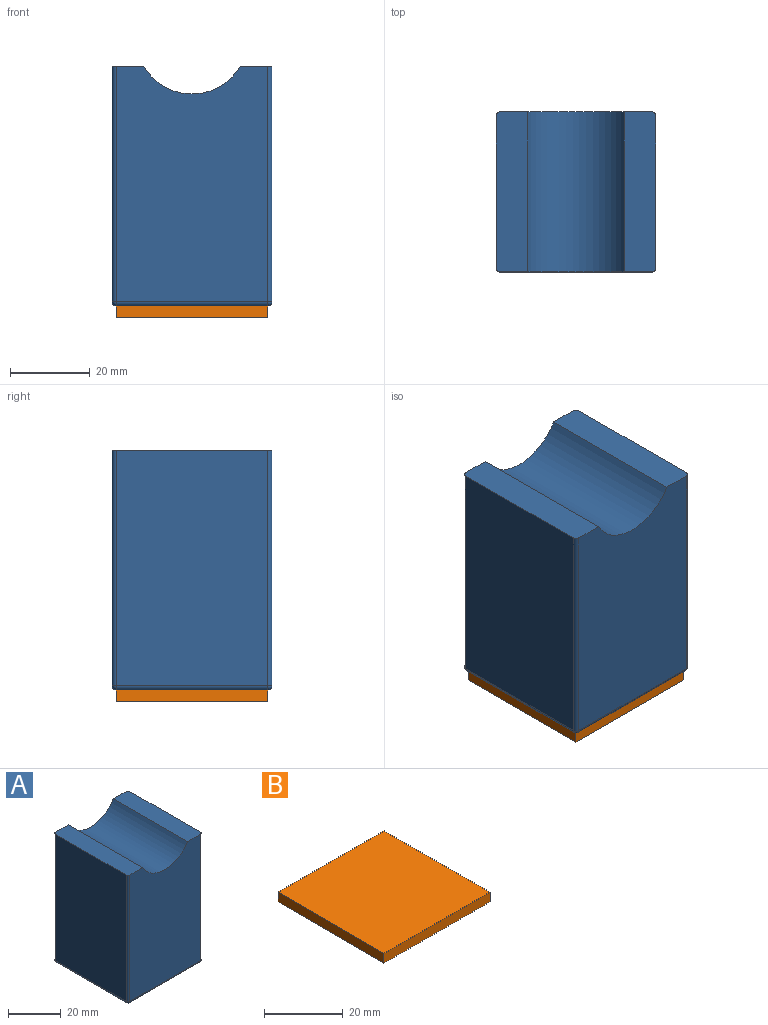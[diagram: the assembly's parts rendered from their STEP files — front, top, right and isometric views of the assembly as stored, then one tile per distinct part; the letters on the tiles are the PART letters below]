
ASSEMBLY  parts=2 mates=1
PART A: 20 faces, bbox 40x40x60 mm
  f0: plane 40x7.88mm, normal (0,0,1), area 314.6mm2, adj f1,f2,f4,f7,f13,f19
  f1: plane 59x38mm, normal (0,1,0), area 2121.6mm2, adj f0,f5,f7,f10,f16,f19
  f2: plane 59x38mm, normal (1,0,0), area 2242mm2, adj f0,f13,f17,f19
  f3: plane 59x38mm, normal (-1,0,0), area 2242mm2, adj f5,f8,f10,f11
  f4: plane 59x38mm, normal (0,-1,0), area 2121.6mm2, adj f0,f5,f7,f8,f12,f13
  f5: plane 40x7.88mm, normal (0,0,1), area 314.6mm2, adj f1,f3,f4,f7,f8,f10
  f6: plane 38x38mm, normal (0,0,-1), area 1444mm2, adj f11,f12,f16,f17
  f7: cylinder r=14mm len=40mm, axis (0,-1,0), area 1172.9mm2, adj f0,f1,f4,f5
  f8: cylinder r=1mm len=59mm, axis (0,0,1), area 92.7mm2, adj f3,f4,f5,f9
  f9: sphere r=1mm, area 1.6mm2, adj f8,f11,f12
  f10: cylinder r=1mm len=59mm, axis (0,0,-1), area 92.7mm2, adj f1,f3,f5,f14
  f11: cylinder r=1mm len=38mm, axis (0,-1,0), area 59.7mm2, adj f3,f6,f9,f14
  f12: cylinder r=1mm len=38mm, axis (1,0,0), area 59.7mm2, adj f4,f6,f9,f15
  f13: cylinder r=1mm len=59mm, axis (0,0,-1), area 92.7mm2, adj f0,f2,f4,f15
  f14: sphere r=1mm, area 1.6mm2, adj f10,f11,f16
  f15: sphere r=1mm, area 1.6mm2, adj f12,f13,f17
  f16: cylinder r=1mm len=38mm, axis (-1,0,0), area 59.7mm2, adj f1,f6,f14,f18
  f17: cylinder r=1mm len=38mm, axis (0,1,0), area 59.7mm2, adj f2,f6,f15,f18
  f18: sphere r=1mm, area 1.6mm2, adj f16,f17,f19
  f19: cylinder r=1mm len=59mm, axis (0,0,1), area 92.7mm2, adj f0,f1,f2,f18
PART B: 6 faces, bbox 38x38x3 mm
  f0: plane 38x3mm, normal (1,0,0), area 114mm2, adj f1,f3,f4,f5
  f1: plane 38x3mm, normal (0,1,0), area 114mm2, adj f0,f2,f4,f5
  f2: plane 38x3mm, normal (-1,0,0), area 114mm2, adj f1,f3,f4,f5
  f3: plane 38x3mm, normal (0,-1,0), area 114mm2, adj f0,f2,f4,f5
  f4: plane 38x38mm, normal (0,0,1), area 1444mm2, adj f0,f1,f2,f3
  f5: plane 38x38mm, normal (0,0,-1), area 1444mm2, adj f0,f1,f2,f3
PLACE A t=(0,0,3)mm
PLACE B at identity
MATE fastened A.f6 <-> B.f4  axis (0,0,-1) through (0,0,3)mm
